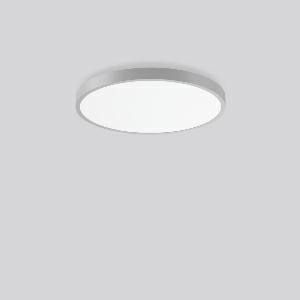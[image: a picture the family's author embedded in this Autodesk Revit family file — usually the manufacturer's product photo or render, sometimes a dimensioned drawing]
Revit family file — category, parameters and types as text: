
# Revit family: triona_round_a_312383_004_2_730_ca99
name_source: partatom
category: Lighting Fixtures
units: mm (PartAtom-declared; Revit-internal decimal feet)

## family parameters
Cut with Voids When Loaded = No
Host = Face
Light Source = No
Part Type = Normal
Room Calculation Point = No
Round Connector Dimension = Use Diameter
Shared = No

## types (1)
- TuneableWhite 846 (1 x LED Modul 846, 3350 lm, 4600)
    Apparent Load = 40 VA
    CIE Flux Codes = 50 80 96 100 100
    Color Rendering = 80
    Color Temperature = 4600
    Default Elevation = 1800 mm
    Description = Series: TRIONA round
Decorative round LED surface-mounted luminaire. Flat, seamless frame: aluminium extrusion profile, powder coated. Cover made of sheet steel, powder-coated. Light emission through a diffuser: plastic, opal. Lightguide and diffuser made of non-yellowing plastic (PMMA). Lateral light emission (RZB SIDELITE technology) for above-average homogeneous light distribution. Tunable white versions, dynamically adjustable from 2700 K to 6500 K. Suitable for Ceiling mounting, Wall (surface). Tool-free mounting via bayonet connection. Electronic ballast included. Very easy installation thanks to Plug+Play connection. With Casambi smart+free Bluetooth control for wireless network and operation using Android / iOS devices, free app available for download. Ideal for use as part of the Human Centric Lighting concept in connection with RZB light management systems. 
Colour: silver, matt (approx. RAL 9006)
Diameter: 681 mm
Height: 88 mm
Lamp: LED
Socket: without socket
Colour temperature: 2700K - 6500K
Colour rendering index (CRI): 80
System power: 40 W
Rated luminous flux: 3350 lm
Luminous efficiency: 84 lm/W
System power 2: 42 W
Rated luminous flux 2: 3200 lm
Luminous efficiency 2: 76 lm/W
System power 3: 42 W
Rated luminous flux 3: 3250 lm
Luminous efficiency 3: 77 lm/W
Control gear: Dimmable Bluetooth converter
Protection class: I
Type of protection: IP 20
    Height = 88 mm
    Lamp = 1 x LED Modul 846
    Lamp Light Flux = 3350 lm
    Lamp count = 1
    Length = 681 mm
    Lifetime = 50000 h
    Luminous efficacy = 84 lm/W
    Manufacturer = RZB
    ModVariant = No
    Model = 312383.004.2.730
    Mounting Place = Ceiling
    Mounting Type = Surface mounted
    Number of Poles = 1
    OnlyDefault = Yes
    Power Factor = 1
    Product Name = TRIONA round A
    Product group = Surface mounted modular luminaires
    ProductGroupID = 306
    Protection Class = Protection class I
    Protection Degree = IP 20
    RLX_Detail_Level = 1
    RLX_Emergency_Light_Flux = 0 lm
    RLX_Emergency_Type = 0
    RLX_Emergency_Type_DB = No
    RlxData = <blob elided: 32561 chars, md5=94713ded>
    Socket = socket
    Standby Power = 0 W
    System Light Flux = 3350 lm
    System Power = 40 W
    Type Comments = TuneableWhite 846
    Type Image = 312384.004.jpg
    URL = http://relux.com
    VarID = tuneablewhite_846
    Voltage = 230 V
    Voltage Range = 220-240 V
    Weight = 0.00 kg
    Width = 0 mm  [stored 0 ft]

note: [stored X ft] marks values corroborated as IEEE doubles in the binary element streams (Revit-internal decimal feet)

## geometry (parser evidence)
native form markers: Blend x4, Sweep x10
no freeform markers — native parametric forms only
